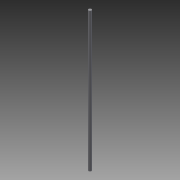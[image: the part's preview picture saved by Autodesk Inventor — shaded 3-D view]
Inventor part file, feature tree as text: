
AUTODESK INVENTOR PART (.ipt)
format: ipt  version: 2013 (Build 170138000, 138)  size: 60,928 bytes
history: native  units: in
note: dims shown in document units (in); Inventor stores cm internally (conversion verified against a paired STEP export)
features: extrude x1, sketch x1
ambient origin geometry x8: Origin, YZ Plane, XZ Plane, XY Plane, X Axis, Y Axis, Z Axis, Center Point
bodies: Solid1 (feature_tree)
feature tree (2):
  extrude  "Extrusion1"  Depth=24.0in TaperAngle=0.0deg
  sketch  "Sketch1"  dims[d0=0.5in d1=24.0in d2=0.0in]
